# Revit family: Midea_VRF_Outdoor_VR_MPanel_V6-R252(280,335)WV2RN1(50Hz) -去LOGO
name_source: partatom
category: Mechanical Equipment
revit_build: Autodesk Revit 2013 (Build: 20120221_2030(x64)
units: mm (PartAtom-declared; Revit-internal decimal feet)

## types (3) — shared parameters
Air Flow = 10000.000 m³/h
Casing color = White
Compressor = 1
Condensation = Air
Depth = 790 mm  [stored 2.59186 ft]
Description = High efficiency air cooled
Gas = R410A
Height = 1635 mm  [stored 5.36417 ft]
High Pressure Gas Pipe = 19.05 mm  [stored 0.0625 ft]
Installation = Outdoor installation
Liquid pipe = 12.7 mm  [stored 0.0416667 ft]
Low Pressure Gas Pipe = 25.4 mm  [stored 0.0833333 ft]
Machine material = Galvanized Steel
Manufacturer = Midea
Net Weight = 232.00 kg
Power supply = 380-415V 3N~50Hz/60Hz
Series = VRF
Width = 990 mm  [stored 3.24803 ft]
clearance access behind = 1000 mm  [stored 3.28084 ft]
clearance access front = 1000 mm  [stored 3.28084 ft]
clearance access left = 1000 mm  [stored 3.28084 ft]
clearance access right = 1000 mm  [stored 3.28084 ft]

## per-type parameters (varying)
| type | Cooling Capacity | Cooling Power Input | Heating Capacity | Heating Power Input | Maximum Fuse Amps | Minimum Circuit Amps |
| MV6-R252WV2RN1 | 22.400 kW | 5.250 kW | 22.400 kW | 3.960 kW | 20 A | 18 A |
| MV6-R280WV2RN1 | 28.000 kW | 7.180 kW | 28.000 kW | 5.460 kW | 25 A | 22 A |
| MV6-R335WV2RN1 | 33.500 kW | 8.640 kW | 33.500 kW | 6.570 kW | 25 A | 24 A |

note: column(s) folded — value = type name in every type: Model

note: [stored X ft] marks values corroborated as IEEE doubles in the binary element streams (Revit-internal decimal feet)

## geometry (parser evidence)
native form markers: Blend x1, Sweep x15
no freeform markers — native parametric forms only
